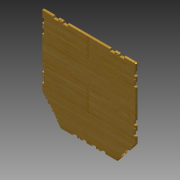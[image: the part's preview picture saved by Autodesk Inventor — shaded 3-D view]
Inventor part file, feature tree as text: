
AUTODESK INVENTOR PART (.ipt)
format: ipt  version: 2014 (Build 180170000, 170)  size: 464,384 bytes
history: native  units: mm
features: hole x11, extrude x8, fillet x6, sketch x3
ambient origin geometry x8: Origin, YZ Plane, XZ Plane, XY Plane, X Axis, Y Axis, Z Axis, Center Point
bodies: Solid1 (feature_tree)
feature tree (28):
  sketch  "Sketch1"  dims[d2=150.0mm d6=200.0mm]
  extrude  "Extrusion1"  Depth=200.0mm
  sketch  "Sketch2"  dims[d7=5.0mm d8=0.0mm d26=25.0mm]
  extrude  "Extrusion2"  Depth=5.0mm
  hole  "Hole11"  [1 undecoded]
  hole  "Hole12"  [1 undecoded]
  hole  "Hole14"  [1 undecoded]
  hole  "Hole17"  [1 undecoded]
  hole  "Hole20"  [1 undecoded]
  fillet  "Fillet8"  Radius=2.5mm
  fillet  "Fillet9"  Radius=2.5mm
  fillet  "Fillet10"  Radius=30.0mm
  fillet  "Fillet11"  Radius=5.0mm
  fillet  "Fillet12"  Radius=2.5mm
  fillet  "Fillet13"  Radius=2.0mm
  sketch  "Sketch3"  dims[d37=30.0mm d41=2.5mm d49=2.0mm d52=2.0mm d53=2.0mm d60=2.0mm d63=2.0mm d64=2.0mm d65=2.5mm d66=2.5mm d74=30.0mm d83=5.0mm d84=0.0mm d147=2.5mm d156=2.0mm d157=2.0mm d158=2.0mm d159=2.0mm d160=35.0mm d161=40.0mm d162=35.0mm d170=3.0mm d171=6.0mm d172=4.0mm d173=2.0mm d174=90.0deg d175=8.0mm d176=20.594885mm d177=3.0mm d178=6.0mm d179=4.0mm d180=2.0mm d181=90.0deg d182=8.0mm d183=20.594885mm d191=30.0mm d195=30.0mm d196=2.5mm d199=2.5mm d200=2.5mm d201=30.0mm d202=27.5mm d203=37.5mm d208=2.0mm d209=2.0mm d210=2.0mm d211=2.0mm d212=2.0mm d213=3.0mm d214=6.0mm d215=4.0mm d216=2.0mm d217=90.0deg d218=8.0mm d219=20.594885mm d234=3.0mm d235=6.0mm d236=4.0mm d237=2.0mm d238=90.0deg d239=8.0mm d240=20.594885mm d248=2.0mm d256=3.0mm d257=6.0mm d258=4.0mm d259=2.0mm d260=90.0deg d261=8.0mm d262=20.594885mm d263=2.0mm d264=2.0mm d265=2.0mm d266=2.0mm d267=2.0mm d268=2.0mm d273=40.0mm d274=40.0mm d275=40.0mm d276=37.5mm d277=120.0mm d278=5.0mm d279=3.0mm d280=6.0mm d281=4.0mm d282=2.0mm d283=90.0deg d284=8.0mm d285=20.594885mm d290=5.0mm d291=0.0mm d293=3.0mm d294=5.0mm d295=0.0mm d296=16.0mm d297=32.0mm d299=3.0mm d304=3.0mm d305=6.0mm d306=4.0mm d307=2.0mm d308=90.0deg d309=8.0mm d310=20.594885mm d311=3.0mm d312=6.0mm d313=4.0mm d314=2.0mm d315=90.0deg d316=8.0mm d317=20.594885mm d318=3.0mm d319=6.0mm d320=4.0mm d321=2.0mm d322=90.0deg d323=8.0mm d324=20.594885mm d325=20.0mm d333=10.0mm d338=10.0mm d342=10.0mm d363=5.0mm d364=10.0mm d365=10.0mm d366=10.0mm d367=25.0mm d368=5.0mm d369=10.0mm d370=10.0mm d371=10.0mm d372=5.0mm d373=0.0mm d381=5.0mm d382=10.0mm d383=10.0mm d384=5.0mm d385=10.0mm d391=25.0mm d392=5.0mm d393=10.0mm d394=10.0mm d395=10.0mm d396=25.0mm d397=5.0mm d398=10.0mm d401=10.0mm d402=10.0mm d403=5.0mm d404=0.0mm d408=2.095mm d434=3.123mm d435=10.0mm d436=2.5mm d437=2.5mm d438=3.123mm d439=10.0mm d440=2.628mm d441=3.123mm d442=10.0mm d443=2.628mm d444=3.123mm d445=10.0mm d446=5.0mm d447=0.0mm d448=20.0mm d449=60.0mm d450=5.0mm d451=10.0mm d453=10.0mm d454=10.0mm d455=5.0mm d456=10.0mm d457=5.0mm d458=0.0mm d459=5.0mm d460=2.5mm d461=3.0mm d462=2.5mm d463=3.0mm d464=3.0mm d465=6.0mm d466=4.0mm d467=2.0mm d468=90.0deg d469=8.0mm d470=20.594885mm d471=3.0mm d472=6.0mm d473=4.0mm d474=2.0mm d475=90.0deg d476=8.0mm d477=20.594885mm]
  hole  "Hole21"  [1 undecoded]
  extrude  "Extrusion5"  Depth=5.0mm
  extrude  "Extrusion6"  Depth=5.0mm
  hole  "Hole22"  [1 undecoded]
  hole  "Hole23"  [1 undecoded]
  hole  "Hole24"  [1 undecoded]
  extrude  "Extrusion13"  Depth=5.0mm
  extrude  "Extrusion16"  Depth=5.0mm
  extrude  "Extrusion19"  Depth=5.0mm
  extrude  "Extrusion20"  Depth=5.0mm
  hole  "Hole25"  [1 undecoded]
  hole  "Hole26"  [1 undecoded]
note: 11 required parameter values undecoded (feature->parameter linkage not recoverable at this tier; creation-order binding heuristic only, values carry confidence <= 0.55)
